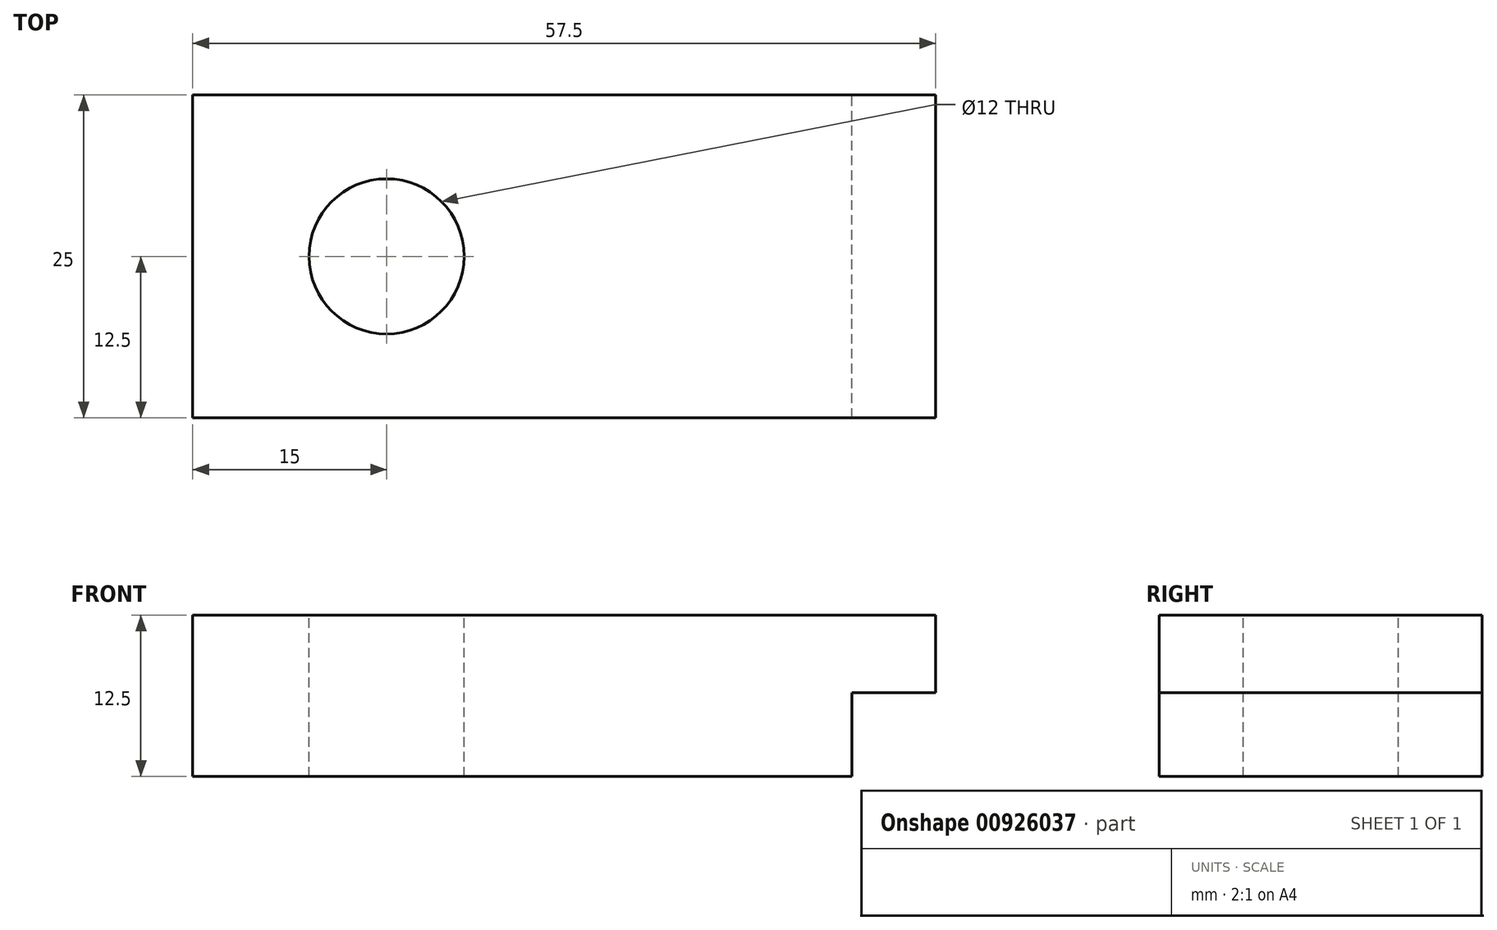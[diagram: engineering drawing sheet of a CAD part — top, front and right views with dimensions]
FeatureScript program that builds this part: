
annotation { "Feature Type Name" : "Feature", "Feature Type Description" : "" }
export const myFeature = defineFeature(function(context is Context, id is Id, definition is map)
    precondition{}
    {
        {
            var Q0;
            Q0=qCreatedBy(makeId("Front.planeOp"),FACE);
            var sketch = newSketch(context, id + "F0", { "sketchPlane" : qUnion([Q0])});
            skLineSegment(sketch, "E0", {"start": v(0, 0) * mm, "end": v(0, 12.5) * mm});
            skLineSegment(sketch, "E1", {"start": v(0, 12.5) * mm, "end": v(57.5, 12.5) * mm});
            skLineSegment(sketch, "E2", {"start": v(57.5, 12.5) * mm, "end": v(57.5, 6.5) * mm});
            skLineSegment(sketch, "E3", {"start": v(57.5, 6.5) * mm, "end": v(51, 6.5) * mm});
            skLineSegment(sketch, "E4", {"start": v(51, 6.5) * mm, "end": v(51, 0) * mm});
            skLineSegment(sketch, "E5", {"start": v(51, 0) * mm, "end": v(0, 0) * mm});
            skSolve(sketch);
        }
        {
            var Q0;
            Q0 = qSketchRegion(id + "F0", true);
            extrude(context, id + "F1", {"entities" : qUnion([Q0]), "depth" : 25 * mm, "offsetDistance" : 25 * mm});
        }
        {
            var Q0;
            Q0=makeQuery(id+"F1.opExtrude","SWEPT_FACE",FACE,{"disambiguationData":[OSD([sQuery(id+"F0.wireOp",EDGE,"E1")])]});
            var sketch = newSketch(context, id + "F2", { "sketchPlane" : qUnion([Q0])});
            skCircle(sketch, "E6", {"center": v(15, -12.5) * mm, "radius": 6 * mm});
            skLineSegment(sketch, "E7", {"start": v(0, -12.5) * mm, "end": v(57.5, -12.5) * mm, "construction": true});
            skLineSegment(sketch, "E8", {"start": v(55, 0) * mm, "end": v(55, -25) * mm, "construction": true});
            skSolve(sketch);
        }
        {
            var Q0;
            Q0 = qSketchRegion(id + "F2", true);
            extrude(context, id + "F3", {"entities" : qUnion([Q0]), "operationType" : NewBodyOperationType.REMOVE, "endBound" : BoundingType.THROUGH_ALL, "oppositeDirection" : true, "depth" : 25 * mm, "offsetDistance" : 25 * mm});
        }
    });
